# Revit family: ASSA ABLOY ZDI
name_source: partatom
category: Mechanical Equipment
revit_build: Autodesk Revit 2018 (Build: 20170223_1515(x64)
units: mm (PartAtom-declared; Revit-internal decimal feet)

## family parameters
Always vertical = Yes
Cut with Voids When Loaded = No
OmniClass Number = 23.75.00.00
OmniClass Title = Climate Control (HVAC)
Part Type = Normal
Room Calculation Point = No
Round Connector Dimension = Use Diameter
Shared = No
Work Plane-Based = No

## types (1)
- ZDI - 469/418/170
    Accessories = https://www.assaabloyglobalsolutions.com
    Article Number = 'Locks needs to be configured *
    Assembly Country = China
    BIM Group ID = ZDI
    Brand = Elsafe
    CB Certificate = https://assaabloy.box.com
    Date of publishing = 10/2/2020
    Depth(mm) = 170 mm  [stored 0.557743 ft]
    Description = Elsafe Zenith Digital In-Wall Safe. Size 469/418/170mm. Internal volume: 17,5 litres. With 3 different body, frame and front colours: black/grey RAL7021, ivory RAL1015,white RAL9003. Weight 20 kilos.
    Design Country = Scandinavia
    DoC = https://assaabloy.box.com
    Edition number = V1.01
    Environmental Management System ISO14001 - EMS 596620 = https://www.assaabloyglobalsolutions.com
    Finish = https://www.assaabloyglobalsolutions.com
    Height(mm) = 469 mm  [stored 1.53871 ft]
    ISO45001 - OHS596621 = https://www.assaabloyglobalsolutions.com
    ISO9001 - FM597854 = https://www.assaabloyglobalsolutions.com
    Main Material = Steel
    Manufacturer = ASSA ABLOY
    Manufacturing Country = China
    NEMKO (EMC) = https://assaabloy.box.com
    Name = Elsafe Zenith In-Wall Safe
    Product Datasheet = https://www.assaabloyglobalsolutions.com
    Product Group = Electronic Safes
    Product Range = Zenith
    Provider = ASSA ABLOY Global Solutions
    Region = Global
    Secondary Material = Polycarbonate
    Similar products from ASSA ABLOY Global Solutions = https://www.assaabloyglobalsolutions.com
    UL Reference Standards = Connect to https://iq.ulprospector.com , create a user FOC and search for ASSA ABLOY Global Solutions to see all our files (i.e the file called GYQS.R19020, you will find our locks and their fire approvals)
    Weight(KG) = 20
    Width(mm) = 418 mm

note: [stored X ft] marks values corroborated as IEEE doubles in the binary element streams (Revit-internal decimal feet)

## geometry (parser evidence)
native form markers: Sweep x2
no freeform markers — native parametric forms only
